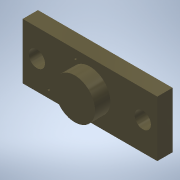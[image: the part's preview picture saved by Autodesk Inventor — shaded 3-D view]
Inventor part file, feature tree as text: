
AUTODESK INVENTOR PART (.ipt)
format: ipt  version: 2020 (Build 240168000, 168)  size: 122,368 bytes
history: mixed  units: in
note: dims shown in document units (in); Inventor stores cm internally (conversion verified against a paired STEP export)
features: other x1, extrude x1, sketch x1, projected_geometry x1, imported_body x1
ambient origin geometry x8: Origin, YZ Plane, XZ Plane, XY Plane, X Axis, Y Axis, Z Axis, Center Point
bodies: Solid1 (imported_parasolid)
feature tree (5):
  other  "Board"
  extrude  "Extrusion1"  Depth=0.0591in TaperAngle=0.0deg
  sketch  "Sketch1"  dims[d0=0.1575in d1=0.0591in d2=0.0in]
  projected_geometry  "Projected Loop1"
  imported_body  NMx_Import_Brep_tag  [imported B-rep: ~18 faces, bbox_mm=[13.238, 5.492, 3.0]]
